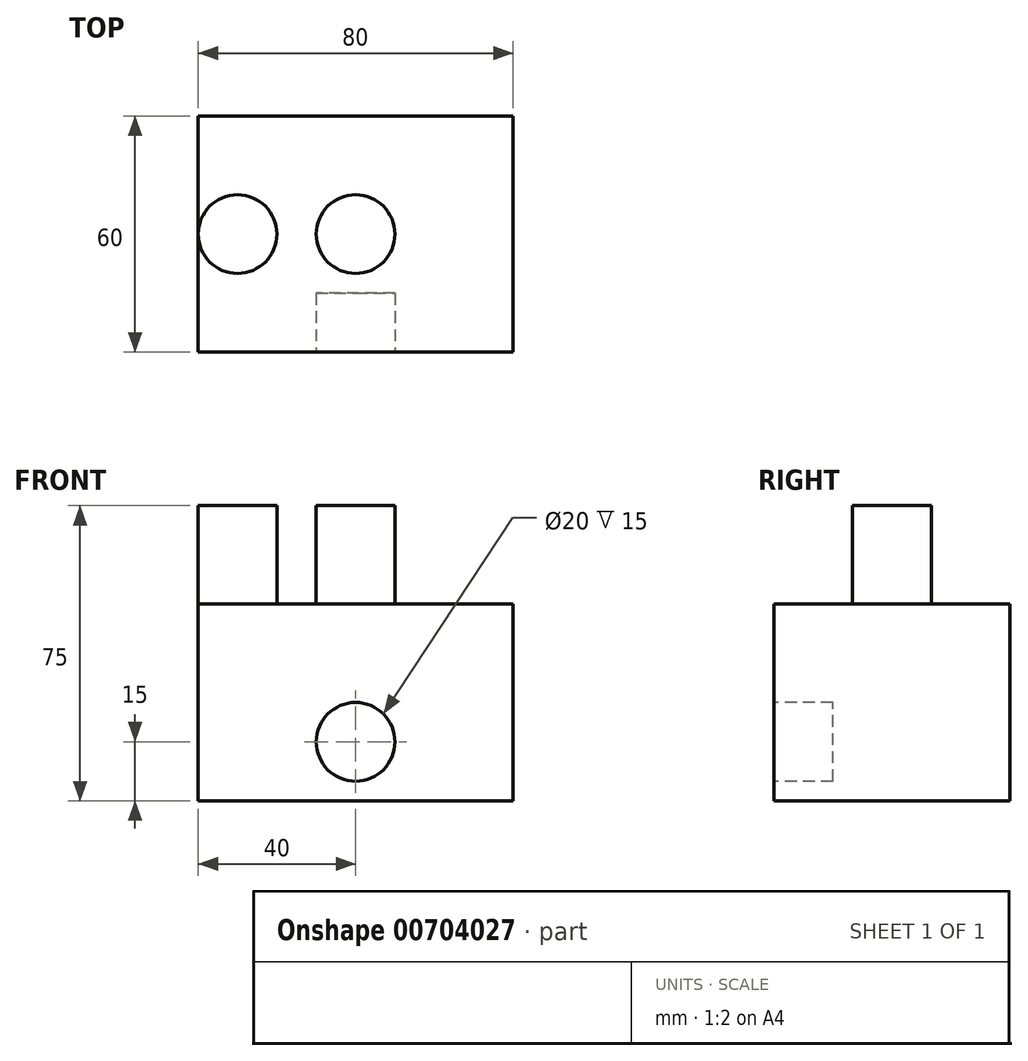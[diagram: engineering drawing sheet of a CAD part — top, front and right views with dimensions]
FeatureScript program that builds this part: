
annotation { "Feature Type Name" : "Feature", "Feature Type Description" : "" }
export const myFeature = defineFeature(function(context is Context, id is Id, definition is map)
    precondition{}
    {
        {
            var Q0;
            Q0=qCreatedBy(makeId("Top.planeOp"),FACE);
            var sketch = newSketch(context, id + "F0", { "sketchPlane" : qUnion([Q0])});
            skLineSegment(sketch, "E0.bottom", {"start": v(40, 30) * mm, "end": v(-40, 30) * mm});
            skLineSegment(sketch, "E0.top", {"start": v(40, -30) * mm, "end": v(-40, -30) * mm});
            skLineSegment(sketch, "E0.left", {"start": v(40, 30) * mm, "end": v(40, -30) * mm});
            skLineSegment(sketch, "E0.right", {"start": v(-40, 30) * mm, "end": v(-40, -30) * mm});
            skPoint(sketch, "E0.middle", {"position": v(0, 0) * mm});
            skSolve(sketch);
        }
        {
            var Q0;
            Q0 = qSketchRegion(id + "F0", true);
            extrude(context, id + "F1", {"entities" : qUnion([Q0]), "depth" : 50 * mm, "offsetDistance" : 25 * mm});
        }
        {
            var Q0;
            Q0=makeQuery(id+"F1.opExtrude","CAP_FACE",FACE,{"disambiguationData":[OSD([sQuery(id+"F0.wireOp",EDGE,"E0.bottom"),sQuery(id+"F0.wireOp",EDGE,"E0.top"),sQuery(id+"F0.wireOp",EDGE,"E0.left"),sQuery(id+"F0.wireOp",EDGE,"E0.right")])],"isStart":false});
            var sketch = newSketch(context, id + "F2", { "sketchPlane" : qUnion([Q0])});
            skCircle(sketch, "E1", {"center": v(-30, 0) * mm, "radius": 10 * mm});
            skSolve(sketch);
        }
        {
            var Q0;
            Q0=makeQuery(id+"F2.imprint","IMPRINT",FACE,{"disambiguationData":[TD([[makeQuery(id+"F2.imprint","IMPRINT",EDGE,{"derivedFrom":sQuery(id+"F2.wireOp",EDGE,"E1")}),1.0]])]});
            extrude(context, id + "F3", {"entities" : qUnion([Q0]), "operationType" : NewBodyOperationType.ADD, "depth" : 25 * mm, "offsetDistance" : 25 * mm});
        }
        {
            var Q0;
            Q0=makeQuery(id+"F1.opExtrude","CAP_FACE",FACE,{"disambiguationData":[OSD([sQuery(id+"F0.wireOp",EDGE,"E0.bottom"),sQuery(id+"F0.wireOp",EDGE,"E0.top"),sQuery(id+"F0.wireOp",EDGE,"E0.left"),sQuery(id+"F0.wireOp",EDGE,"E0.right")])],"isStart":false});
            var sketch = newSketch(context, id + "F4", { "sketchPlane" : qUnion([Q0])});
            skCircle(sketch, "E2", {"center": v(0, 0) * mm, "radius": 10 * mm});
            skSolve(sketch);
        }
        {
            var Q0;
            Q0 = qSketchRegion(id + "F4", true);
            extrude(context, id + "F5", {"entities" : qUnion([Q0]), "operationType" : NewBodyOperationType.ADD, "depth" : 25 * mm, "offsetDistance" : 25 * mm});
        }
        {
            var Q0;
            Q0=makeQuery(id+"F1.opExtrude","SWEPT_FACE",FACE,{"disambiguationData":[OSD([sQuery(id+"F0.wireOp",EDGE,"E0.top")])]});
            var sketch = newSketch(context, id + "F6", { "sketchPlane" : qUnion([Q0])});
            skCircle(sketch, "E3", {"center": v(0, 15) * mm, "radius": 10 * mm});
            skSolve(sketch);
        }
        {
            var Q0;
            Q0 = qSketchRegion(id + "F6", true);
            extrude(context, id + "F7", {"entities" : qUnion([Q0]), "operationType" : NewBodyOperationType.REMOVE, "oppositeDirection" : true, "depth" : 15 * mm, "offsetDistance" : 25 * mm});
        }
    });
